# Revit family: A_1
name_source: partatom
category: Plumbing Fixtures
units: mm (PartAtom-declared; Revit-internal decimal feet)

## family parameters
Cut with Voids When Loaded = No
Host = Face
OmniClass Number = 23.31.11.00
Part Type = Normal
Room Calculation Point = No
Round Connector Dimension = Use Diameter
Shared = No

## types (6) — shared parameters
ADA Compliant = No
Assembly Code = D2010
CW Connection = No
Cold Water Inlet = Cold Water Inlet
Date Modified = 11/06/2024
Default Elevation = 36"
Description = Wall Mount Bath Spout
Drain Included = Yes
Flow Rate = 0 GPM
HW Connection = Yes
Height = 2 3/8"
Hot Water Inlet = Hot Water Inlet
Length = 7 1/8"
Manufacturer = Kallista Co.
Master Format 2014 = 22 41 39
Master Format 2014 Name = Residential Faucets, Supplies, and Trim
Material = Premium Metal Construction
Pressure = 0.00 psi
Product Name = Italy
Spout Reach = 7 1/8"
Tempered Water Inlet = Tempered Water Inlet
URL = https://www.kallista.com
Vent Connection = No
Waste Connection = No
Waste Water Outlet = Waste Water Outlet
WaterSense Certified = No
Width = 3 1/8"

## per-type parameters (varying)
| type | Finish | Model | Type |
| 2MB-Brushed Brass | Kallista-Metal-2MB- Brushed_Brass | P32714-00-2MB | 1 |
| BGP-Brushed Graphite | Kallista-Metal-BGP-Brushed_Graphite | P32714-00-BGP | 2 |
| BN-Brushed Nickel | Kallista-Metal-BN-Brushed_Nickel | P32714-00-BN | 3 |
| CP-Chrome | Kallista-Metal-CP-Chrome | P32714-00-CP | 4 |
| PGP-Polished Graphite | Kallista-Metal-PGP-Polished_Graphite | P32714-00-PGP | 5 |
| BLH-Blush Brass | Kallista-Metal-BLH-Blush_Brass | P32714-00-BLH | 6 |

## geometry (parser evidence)
native form markers: Sweep x6
no freeform markers — native parametric forms only
